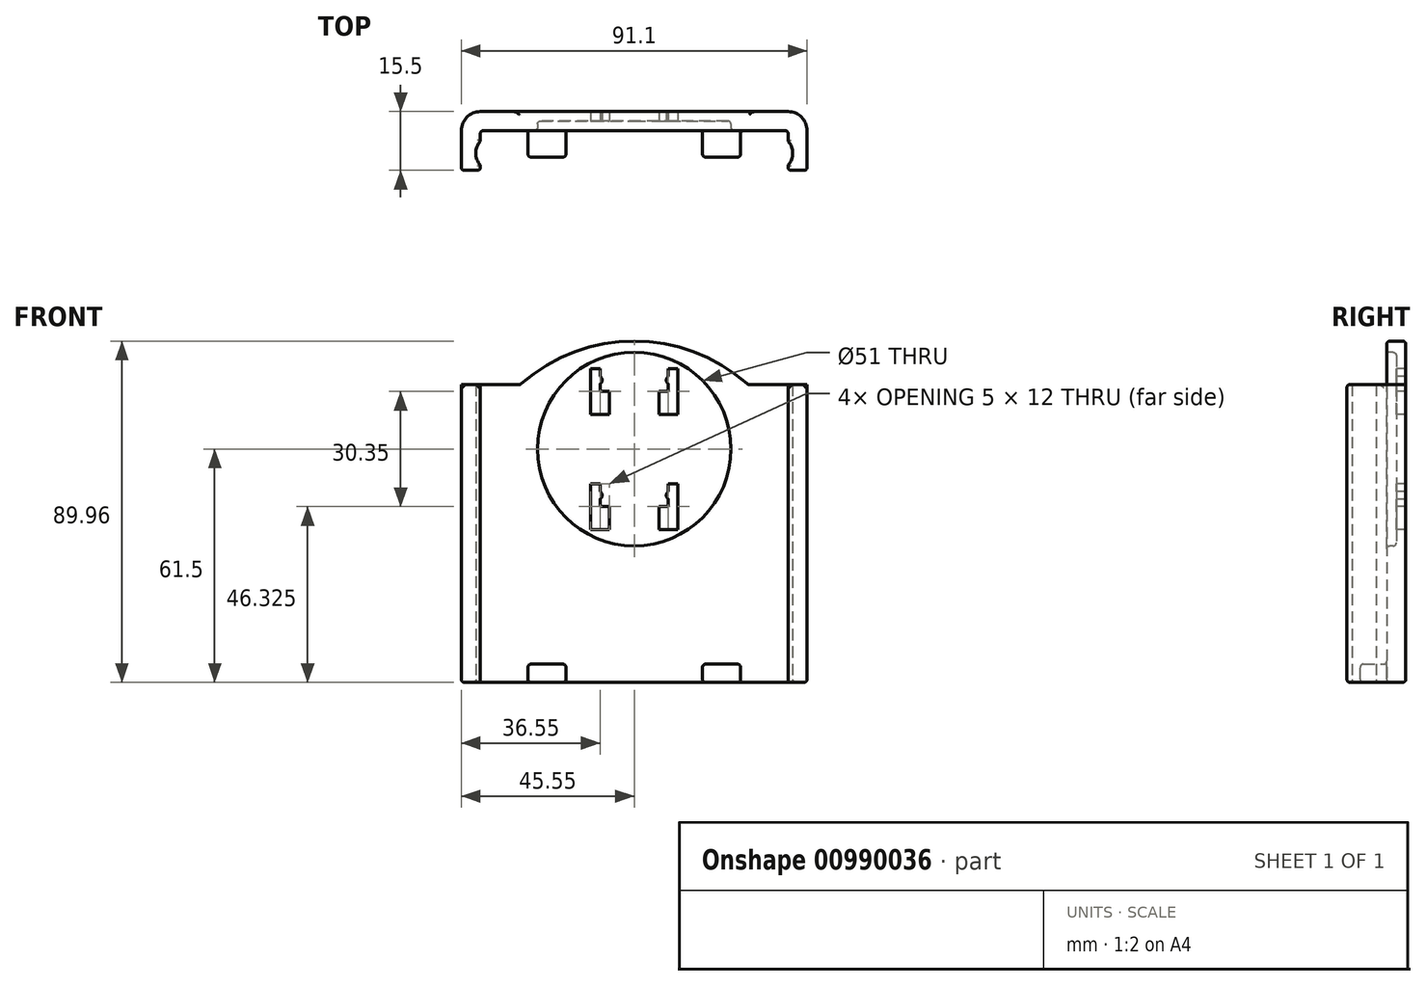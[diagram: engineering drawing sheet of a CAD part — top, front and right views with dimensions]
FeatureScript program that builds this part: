
annotation { "Feature Type Name" : "Feature", "Feature Type Description" : "" }
export const myFeature = defineFeature(function(context is Context, id is Id, definition is map)
    precondition{}
    {
        {
            assignVariable(context, id + "F0", {"name" : "PhoneCasing_Thickness", "anyValue" : 10.5});
        }
        {
            assignVariable(context, id + "F1", {"name" : "Casing_LengthUnderVolKeys", "anyValue" : 73.5});
        }
        {
            assignVariable(context, id + "F2", {"name" : "Clip_Depth", "anyValue" : 4.5});
        }
        {
            assignVariable(context, id + "F3", {"name" : "Clip_Thickness", "anyValue" : 2});
        }
        {
            var Q0;
            Q0=qCreatedBy(makeId("Top.planeOp"),FACE);
            var sketch = newSketch(context, id + "F4", { "sketchPlane" : qUnion([Q0])});
            skLineSegment(sketch, "E0", {"start": v(-45.55, 0) * mm, "end": v(45.55, 0) * mm});
            skLineSegment(sketch, "E1", {"start": v(45.55, 0) * mm, "end": v(45.55, -15.5) * mm});
            skLineSegment(sketch, "E2", {"start": v(45.55, -15.5) * mm, "end": v(40.55, -15.5) * mm});
            skLineSegment(sketch, "E3", {"start": v(40.55, -15.5) * mm, "end": v(40.55, -14.1) * mm});
            skLineSegment(sketch, "E4", {"start": v(40.55, -5) * mm, "end": v(-40.55, -5) * mm});
            skLineSegment(sketch, "E5", {"start": v(-40.55, -5) * mm, "end": v(-40.55, -7.8) * mm});
            skLineSegment(sketch, "E6", {"start": v(-40.55, -15.5) * mm, "end": v(-45.55, -15.5) * mm});
            skLineSegment(sketch, "E7", {"start": v(-45.55, -15.5) * mm, "end": v(-45.55, 0) * mm});
            skArc(sketch, "E8", {"start": v(-40.55, -7.8) * mm, "mid": v(-41.75, -10.95) * mm, "end": v(-40.55, -14.1) * mm});
            skPoint(sketch, "E9", {"position": v(-41.75, -10.95) * mm});
            skLineSegment(sketch, "E10.trimOffspring", {"start": v(-40.55, -14.1) * mm, "end": v(-40.55, -15.5) * mm});
            skArc(sketch, "E11.MirrorCS", {"start": v(40.55, -7.8) * mm, "mid": v(41.75, -10.95) * mm, "end": v(40.55, -14.1) * mm});
            skLineSegment(sketch, "E12.trimOffspring", {"start": v(40.55, -7.8) * mm, "end": v(40.55, -5) * mm});
            skSolve(sketch);
        }
        {
            var Q0;
            Q0 = qSketchRegion(id + "F4", true);
            extrude(context, id + "F5", {"entities" : qUnion([Q0]), "depth" : (getVariable(context, 'Casing_LengthUnderVolKeys') + 5) * mm, "offsetDistance" : 25 * mm});
        }
        {
            var Q0;
            Q0=makeQuery(id+"F5.opExtrude","SWEPT_FACE",FACE,{"disambiguationData":[OSD([sQuery(id+"F4.wireOp",EDGE,"E4")])]});
            var sketch = newSketch(context, id + "F6", { "sketchPlane" : qUnion([Q0])});
            skLineSegment(sketch, "E13.bottom", {"start": v(-28, 0) * mm, "end": v(-18, 0) * mm});
            skLineSegment(sketch, "E13.top", {"start": v(-28, 4.8) * mm, "end": v(-18, 4.8) * mm});
            skLineSegment(sketch, "E13.left", {"start": v(-28, 0) * mm, "end": v(-28, 4.8) * mm});
            skLineSegment(sketch, "E13.right", {"start": v(-18, 0) * mm, "end": v(-18, 4.8) * mm});
            skLineSegment(sketch, "E14.MirrorCS", {"start": v(28, 4.8) * mm, "end": v(18, 4.8) * mm});
            skLineSegment(sketch, "E15.MirrorCS", {"start": v(18, 0) * mm, "end": v(18, 4.8) * mm});
            skLineSegment(sketch, "E16.MirrorCS", {"start": v(28, 0) * mm, "end": v(18, 0) * mm});
            skLineSegment(sketch, "E17.MirrorCS", {"start": v(28, 0) * mm, "end": v(28, 4.8) * mm});
            skSolve(sketch);
        }
        {
            var Q0;
            Q0 = qSketchRegion(id + "F6", true);
            extrude(context, id + "F7", {"entities" : qUnion([Q0]), "operationType" : NewBodyOperationType.ADD, "depth" : (getVariable(context, 'PhoneCasing_Thickness') / 3 * 2) * mm, "offsetDistance" : 25 * mm});
        }
        {
            var Q0;
            Q0=makeQuery(id+"F5.opExtrude","SWEPT_FACE",FACE,{"disambiguationData":[OSD([sQuery(id+"F4.wireOp",EDGE,"E0")])]});
            var sketch = newSketch(context, id + "F8", { "sketchPlane" : qUnion([Q0])});
            skArc(sketch, "E18", {"start": v(30, 78.5) * mm, "mid": v(0, 89.96) * mm, "end": v(-30, 78.5) * mm});
            skLineSegment(sketch, "E19", {"start": v(-30, 78.5) * mm, "end": v(30, 78.5) * mm});
            skPoint(sketch, "E20", {"position": v(0, 78.5) * mm});
            skSolve(sketch);
        }
        {
            var Q0;
            Q0 = qSketchRegion(id + "F8", true);
            extrude(context, id + "F9", {"entities" : qUnion([Q0]), "operationType" : NewBodyOperationType.ADD, "oppositeDirection" : true, "depth" : (getVariable(context, 'Clip_Depth') + 0.5) * mm, "offsetDistance" : 25 * mm});
        }
        {
            var Q0;
            Q0=makeQuery(id+"F5.opExtrude","SWEPT_FACE",FACE,{"disambiguationData":[OSD([sQuery(id+"F4.wireOp",EDGE,"E4")])]});
            var sketch = newSketch(context, id + "F10", { "sketchPlane" : qUnion([Q0])});
            skCircle(sketch, "E21", {"center": v(0, 61.5) * mm, "radius": 25.5 * mm});
            skLineSegment(sketch, "E22", {"start": v(0, 61.5) * mm, "end": v(-40.55, 61.5) * mm, "construction": true});
            skLineSegment(sketch, "E23", {"start": v(0, 61.5) * mm, "end": v(40.55, 61.5) * mm, "construction": true});
            skSolve(sketch);
        }
        {
            var Q0;
            Q0 = qSketchRegion(id + "F10", true);
            extrude(context, id + "F11", {"entities" : qUnion([Q0]), "operationType" : NewBodyOperationType.REMOVE, "endBound" : BoundingType.UP_TO_NEXT, "oppositeDirection" : true, "depth" : 25 * mm, "hasOffset" : true, "offsetDistance" : (getVariable(context, 'Clip_Depth') - getVariable(context, 'Clip_Thickness')) * mm});
        }
        {
            var Q0;
            Q0=makeQuery(id+"F11.boolean.opBoolean","COPY",FACE,{"derivedFrom":makeQuery(id+"F11.opExtrude","CAP_FACE",FACE,{"disambiguationData":[OSD([sQuery(id+"F10.wireOp",EDGE,"E21")])],"isStart":false})});
            var sketch = newSketch(context, id + "F12", { "sketchPlane" : qUnion([Q0])});
            skLineSegment(sketch, "E24", {"start": v(-11.5, 82.68) * mm, "end": v(-11.5, 70.67) * mm});
            skLineSegment(sketch, "E25", {"start": v(-11.5, 70.68) * mm, "end": v(-6.5, 70.68) * mm});
            skLineSegment(sketch, "E26", {"start": v(-6.5, 70.67) * mm, "end": v(-6.5, 76.68) * mm});
            skPoint(sketch, "E26.endSnap0", {"position": v(-11.5, 76.68) * mm});
            skLineSegment(sketch, "E27", {"start": v(-6.5, 76.68) * mm, "end": v(-9, 76.68) * mm});
            skPoint(sketch, "E27.endSnap0", {"position": v(-9, 70.68) * mm});
            skLineSegment(sketch, "E28", {"start": v(-9, 76.68) * mm, "end": v(-9, 78.68) * mm});
            skLineSegment(sketch, "E29", {"start": v(-9, 82.68) * mm, "end": v(-11.5, 82.68) * mm});
            skArc(sketch, "E30", {"start": v(-9, 78.68) * mm, "mid": v(-8.46, 79.68) * mm, "end": v(-9, 80.68) * mm});
            skLineSegment(sketch, "E31.trimOffspring", {"start": v(-9, 80.68) * mm, "end": v(-9, 82.68) * mm});
            skLineSegment(sketch, "E32.1.0.0", {"start": v(-9, 52.33) * mm, "end": v(-11.5, 52.33) * mm});
            skLineSegment(sketch, "E32.1.0.1", {"start": v(-11.5, 52.33) * mm, "end": v(-11.5, 40.33) * mm});
            skLineSegment(sketch, "E32.1.0.2", {"start": v(-11.5, 40.33) * mm, "end": v(-6.5, 40.33) * mm});
            skLineSegment(sketch, "E32.1.0.3", {"start": v(-6.5, 40.33) * mm, "end": v(-6.5, 46.33) * mm});
            skLineSegment(sketch, "E32.1.0.4", {"start": v(-6.5, 46.33) * mm, "end": v(-9, 46.33) * mm});
            skLineSegment(sketch, "E32.1.0.5", {"start": v(-9, 46.33) * mm, "end": v(-9, 48.33) * mm});
            skArc(sketch, "E32.1.0.6", {"start": v(-9, 48.33) * mm, "mid": v(-8.46, 49.33) * mm, "end": v(-9, 50.33) * mm});
            skLineSegment(sketch, "E32.1.0.7", {"start": v(-9, 50.33) * mm, "end": v(-9, 52.33) * mm});
            skLineSegment(sketch, "E32.direction1", {"start": v(-11.5, 82.68) * mm, "end": v(-11.5, 52.33) * mm, "construction": true});
            skLineSegment(sketch, "E33.MirrorCS", {"start": v(11.5, 70.68) * mm, "end": v(6.5, 70.68) * mm});
            skLineSegment(sketch, "E34.MirrorCS", {"start": v(9, 82.68) * mm, "end": v(11.5, 82.68) * mm});
            skPoint(sketch, "E35.MirrorP", {"position": v(9, 70.68) * mm});
            skArc(sketch, "E36.MirrorCS", {"start": v(9, 78.68) * mm, "mid": v(8.46, 79.68) * mm, "end": v(9, 80.68) * mm});
            skLineSegment(sketch, "E37.MirrorCS", {"start": v(9, 80.68) * mm, "end": v(9, 82.68) * mm});
            skLineSegment(sketch, "E38.MirrorCS", {"start": v(11.5, 82.68) * mm, "end": v(11.5, 70.67) * mm});
            skLineSegment(sketch, "E39.MirrorCS", {"start": v(6.5, 70.67) * mm, "end": v(6.5, 76.68) * mm});
            skLineSegment(sketch, "E40.MirrorCS", {"start": v(6.5, 76.68) * mm, "end": v(9, 76.68) * mm});
            skLineSegment(sketch, "E41.MirrorCS", {"start": v(9, 76.68) * mm, "end": v(9, 78.68) * mm});
            skPoint(sketch, "E42.MirrorP", {"position": v(11.5, 76.68) * mm});
            skLineSegment(sketch, "E43.MirrorCS", {"start": v(6.5, 40.33) * mm, "end": v(6.5, 46.33) * mm});
            skLineSegment(sketch, "E44.MirrorCS", {"start": v(9, 46.33) * mm, "end": v(9, 48.33) * mm});
            skLineSegment(sketch, "E45.MirrorCS", {"start": v(11.5, 40.33) * mm, "end": v(6.5, 40.33) * mm});
            skLineSegment(sketch, "E46.MirrorCS", {"start": v(9, 52.33) * mm, "end": v(11.5, 52.33) * mm});
            skLineSegment(sketch, "E47.MirrorCS", {"start": v(6.5, 46.33) * mm, "end": v(9, 46.33) * mm});
            skLineSegment(sketch, "E48.MirrorCS", {"start": v(11.5, 52.33) * mm, "end": v(11.5, 40.33) * mm});
            skArc(sketch, "E49.MirrorCS", {"start": v(9, 48.33) * mm, "mid": v(8.46, 49.33) * mm, "end": v(9, 50.33) * mm});
            skLineSegment(sketch, "E50.MirrorCS", {"start": v(9, 50.33) * mm, "end": v(9, 52.33) * mm});
            skLineSegment(sketch, "E51", {"start": v(-11.5, 82.68) * mm, "end": v(11.5, 40.33) * mm, "construction": true});
            skPoint(sketch, "E52", {"position": v(0, 61.5) * mm});
            skSolve(sketch);
        }
        {
            var Q0;
            Q0 = qSketchRegion(id + "F12", true);
            extrude(context, id + "F13", {"entities" : qUnion([Q0]), "operationType" : NewBodyOperationType.REMOVE, "endBound" : BoundingType.UP_TO_NEXT, "oppositeDirection" : true, "depth" : 25 * mm, "offsetDistance" : 25 * mm});
        }
        {
            var Q0;
            Q0=makeQuery(id+"F5.opExtrude","SWEPT_EDGE",EDGE,{"disambiguationData":[OSD([sQuery(id+"F4.wireOp",EDGE,"E0"),sQuery(id+"F4.wireOp",EDGE,"E7")])]});
            var Q1;
            Q1=makeQuery(id+"F5.opExtrude","SWEPT_EDGE",EDGE,{"disambiguationData":[OSD([sQuery(id+"F4.wireOp",EDGE,"E0"),sQuery(id+"F4.wireOp",EDGE,"E1")])]});
            fillet(context, id + "F14", {"entities" : qUnion([Q0, Q1]), "radius" : 5 * mm, "tangentPropagation" : true, "allowEdgeOverflow" : false});
        }
        {
            var Q0;
            Q0=makeQuery(id+"F9.opExtrude","SWEPT_FACE",FACE,{"disambiguationData":[OSD([sQuery(id+"F8.wireOp",EDGE,"E18")])]});
            var Q1;
            Q1=makeQuery(id+"F5.opExtrude","SWEPT_FACE",FACE,{"disambiguationData":[OSD([sQuery(id+"F4.wireOp",EDGE,"E2")])]});
            var Q2;
            Q2=makeQuery(id+"F5.opExtrude","SWEPT_FACE",FACE,{"disambiguationData":[OSD([sQuery(id+"F4.wireOp",EDGE,"E6")])]});
            var Q3;
            Q3=makeQuery(id+"F9.boolean.opBoolean","MERGE",FACE,{"derivedFrom":[makeQuery(id+"F5.opExtrude","SWEPT_FACE",FACE,{"disambiguationData":[OSD([sQuery(id+"F4.wireOp",EDGE,"E4")])]}),makeQuery(id+"F9.opExtrude","CAP_FACE",FACE,{"disambiguationData":[OSD([sQuery(id+"F8.wireOp",EDGE,"E18"),sQuery(id+"F8.wireOp",EDGE,"E19")])],"isStart":false})]});
            var Q4;
            Q4=makeQuery(id+"F11.boolean.opBoolean","COPY",EDGE,{"derivedFrom":makeQuery(id+"F11.opExtrude","CAP_EDGE",EDGE,{"disambiguationData":[OSD([sQuery(id+"F10.wireOp",EDGE,"E21")])],"isStart":false})});
            var Q5;
            Q5=makeQuery(id+"F7.boolean.opBoolean","MERGE",FACE,{"derivedFrom":[makeQuery(id+"F5.opExtrude","CAP_FACE",FACE,{"disambiguationData":[OSD([sQuery(id+"F4.wireOp",EDGE,"E0"),sQuery(id+"F4.wireOp",EDGE,"E1"),sQuery(id+"F4.wireOp",EDGE,"E2"),sQuery(id+"F4.wireOp",EDGE,"E3"),sQuery(id+"F4.wireOp",EDGE,"E4"),sQuery(id+"F4.wireOp",EDGE,"E5"),sQuery(id+"F4.wireOp",EDGE,"E6"),sQuery(id+"F4.wireOp",EDGE,"E7"),sQuery(id+"F4.wireOp",EDGE,"E8"),sQuery(id+"F4.wireOp",EDGE,"E10.trimOffspring"),sQuery(id+"F4.wireOp",EDGE,"E11.MirrorCS"),sQuery(id+"F4.wireOp",EDGE,"E12.trimOffspring")])],"isStart":true}),makeQuery(id+"F7.opExtrude","SWEPT_FACE",FACE,{"disambiguationData":[OSD([sQuery(id+"F6.wireOp",EDGE,"E13.bottom")])]}),makeQuery(id+"F7.opExtrude","SWEPT_FACE",FACE,{"disambiguationData":[OSD([sQuery(id+"F6.wireOp",EDGE,"E16.MirrorCS")])]})]});
            var Q6;
            Q6=makeQuery(id+"F7.opExtrude","CAP_FACE",FACE,{"disambiguationData":[OSD([sQuery(id+"F6.wireOp",EDGE,"E14.MirrorCS"),sQuery(id+"F6.wireOp",EDGE,"E15.MirrorCS"),sQuery(id+"F6.wireOp",EDGE,"E16.MirrorCS"),sQuery(id+"F6.wireOp",EDGE,"E17.MirrorCS")])],"isStart":false});
            var Q7;
            Q7=makeQuery(id+"F7.opExtrude","CAP_FACE",FACE,{"disambiguationData":[OSD([sQuery(id+"F6.wireOp",EDGE,"E13.bottom"),sQuery(id+"F6.wireOp",EDGE,"E13.top"),sQuery(id+"F6.wireOp",EDGE,"E13.left"),sQuery(id+"F6.wireOp",EDGE,"E13.right")])],"isStart":false});
            var Q8;
            Q8=makeQuery(id+"F7.opExtrude","SWEPT_FACE",FACE,{"disambiguationData":[OSD([sQuery(id+"F6.wireOp",EDGE,"E13.top")])]});
            var Q9;
            Q9=makeQuery(id+"F7.opExtrude","SWEPT_FACE",FACE,{"disambiguationData":[OSD([sQuery(id+"F6.wireOp",EDGE,"E14.MirrorCS")])]});
            fillet(context, id + "F15", {"entities" : qUnion([Q0, Q1, Q2, Q3, Q4, Q5, Q6, Q7, Q8, Q9]), "radius" : 0.8 * mm, "tangentPropagation" : true, "allowEdgeOverflow" : false});
        }
    });
